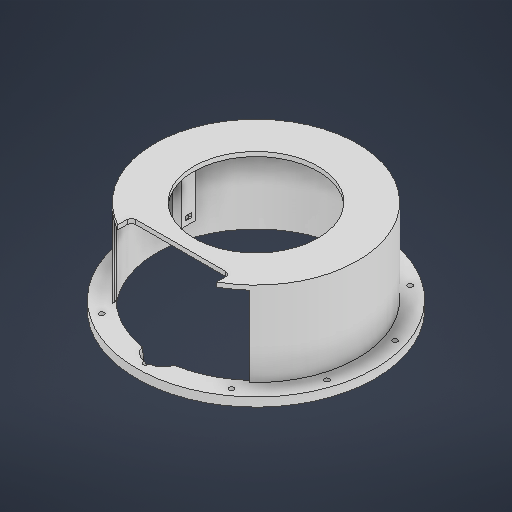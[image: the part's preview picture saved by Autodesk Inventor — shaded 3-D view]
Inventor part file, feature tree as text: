
AUTODESK INVENTOR PART (.ipt)
format: ipt  version: 2025 (Build 290162000, 162)  size: 398,336 bytes
history: native  units: in
note: dims shown in document units (in); Inventor stores cm internally (conversion verified against a paired STEP export)
features: sketch x10, extrude x10, plane x3, fillet x1
ambient origin geometry x8: Origin, YZ Plane, XZ Plane, XY Plane, X Axis, Y Axis, Z Axis, Center Point
bodies: Solid1 (feature_tree)
feature tree (24):
  sketch  "Sketch1"  dims[d5=0.0in d7=0.0in]
  extrude  "Extrusion1"  TaperAngle=0.0deg  [1 undecoded]
  extrude  "Extrusion2"  Depth=4.5276in
  extrude  "Extrusion7"  Depth=0.2165in
  extrude  "Extrusion34"  Depth=6.1024in
  sketch  "Sketch30"  dims[d272=3.937in d273=4.1535in d274=0.0in d285=3.937in]
  plane  "Work Plane19"
  plane  "Work Plane21"
  plane  "Work Plane22"
  extrude  "Extrusion36"  Depth=4.1535in TaperAngle=0.0deg
  fillet  "Fillet19"  Radius=3.937in
  extrude  "Extrusion37"  Depth=2.0812in TaperAngle=0.0deg
  extrude  "Extrusion38"  Depth=0.1969in
  sketch  "Sketch35"  dims[d293=0.1969in d294=0.1969in]
  extrude  "Extrusion40"  Depth=4.4094in
  extrude  "Extrusion41"  Depth=0.1969in
  extrude  "Extrusion42"  Depth=0.3937in TaperAngle=0.0deg
  sketch  "Sketch2"  dims[d18=0.0in d52=4.5276in]
  sketch  "Sketch Circular Pattern5"  dims[d264=9.8425in d265=0.2165in]
  sketch  "Sketch28"  dims[d266=3.937in d268=360.0deg d271=6.1024in]
  sketch  "Sketch31"  dims[d286=1.5748in d287=2.0812in d288=0.0in]
  sketch  "Sketch32"  dims[d289=3.5039in d290=0.1969in]
  sketch  "Sketch33"  dims[d291=4.4094in d292=1.5748in]
  sketch  "Sketch36"  dims[d295=3.3465in d296=0.3937in d297=0.0in d298=0.6299in d299=1.7717in d300=0.0in d301=2.9528in d308=6.378in d309=0.2805in d310=0.5906in d311=0.0in d312=6.8898in d313=5.5413in d314=0.2362in d315=0.1969in d316=0.0in d317=0.1969in d318=0.0in d113=0.0197in d114=0.0344in d115=0.0197in d116=0.0344in d167=0.0197in d168=0.0344in d169=0.0197in d170=0.0344in d215=0.0197in d216=0.0344in d217=0.0197in d218=0.0344in d219=0.0in d220=0.0in d254=0.0197in d255=0.0344in d256=0.0197in d257=0.0344in]
note: 1 required parameter value undecoded (feature->parameter linkage not recoverable at this tier; creation-order binding heuristic only, values carry confidence <= 0.55)
